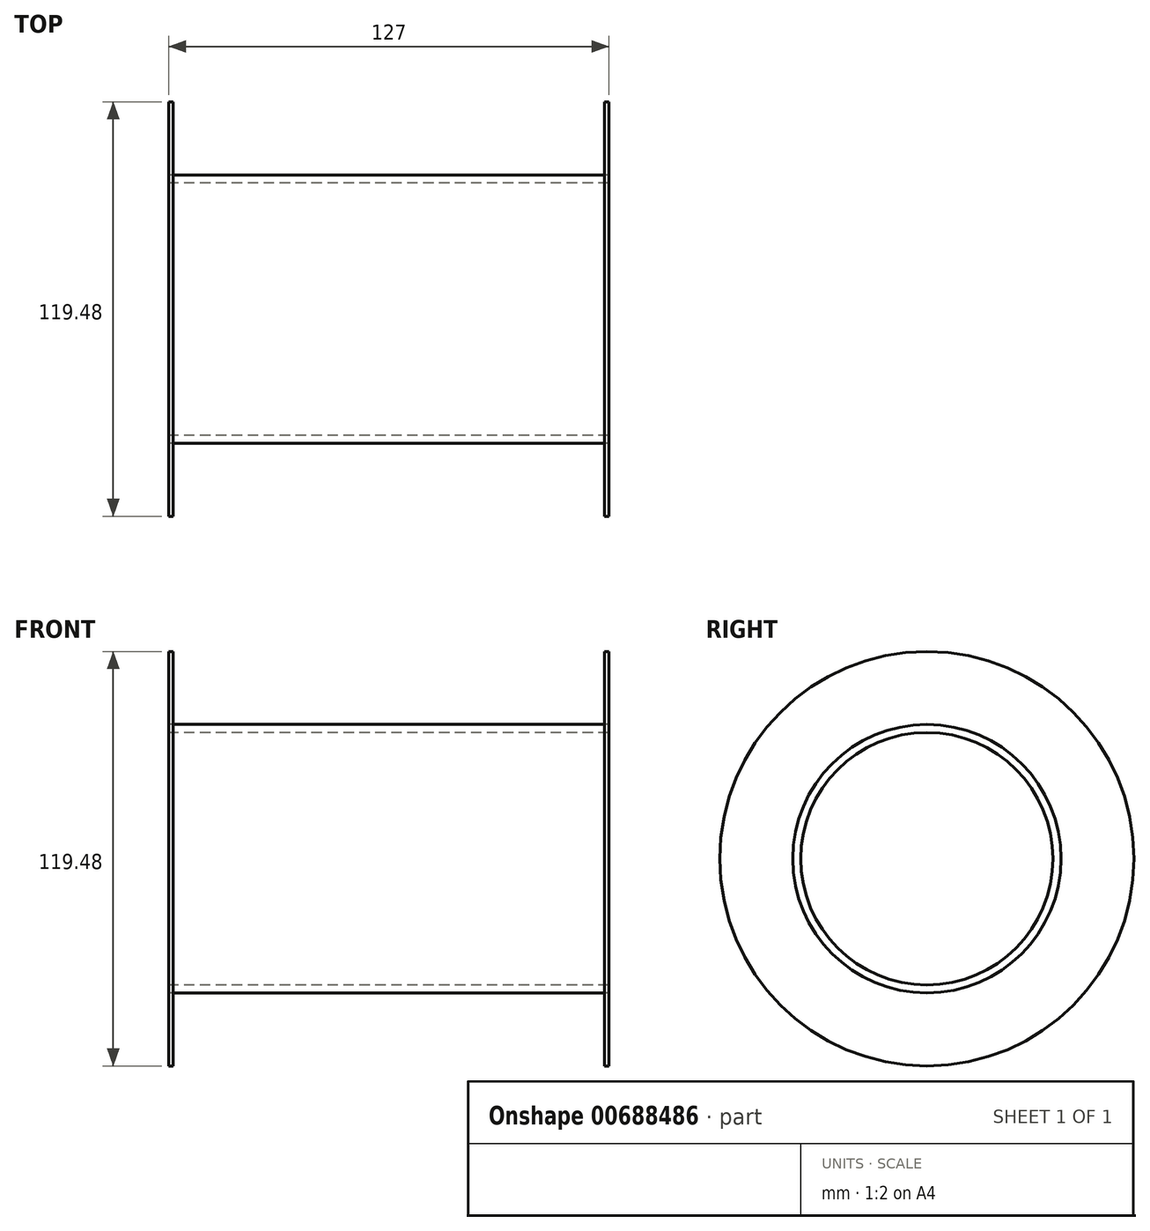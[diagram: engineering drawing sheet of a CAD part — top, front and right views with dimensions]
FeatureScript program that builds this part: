
annotation { "Feature Type Name" : "Feature", "Feature Type Description" : "" }
export const myFeature = defineFeature(function(context is Context, id is Id, definition is map)
    precondition{}
    {
        {
            var Q0;
            Q0=qCreatedBy(makeId("Right.planeOp"),FACE);
            var sketch = newSketch(context, id + "F0", { "sketchPlane" : qUnion([Q0])});
            skCircle(sketch, "E0", {"center": v(0, 0) * mm, "radius": 38.7 * mm});
            skCircle(sketch, "E1", {"center": v(0, 0) * mm, "radius": 36.39 * mm});
            skSolve(sketch);
        }
        {
            var Q0;
            Q0 = qSketchRegion(id + "F0", true);
            extrude(context, id + "F1", {"entities" : qUnion([Q0]), "endBound" : BoundingType.SYMMETRIC, "depth" : 127 * mm, "offsetDistance" : 25.4 * mm});
        }
        {
            var Q0;
            Q0=qCreatedBy(makeId("Front.planeOp"),FACE);
            var sketch = newSketch(context, id + "F2", { "sketchPlane" : qUnion([Q0])});
            skLineSegment(sketch, "E2", {"start": v(-74.68, 0) * mm, "end": v(76.9, 0) * mm, "construction": true});
            skLineSegment(sketch, "E3", {"start": v(0, 0) * mm, "end": v(0, 75.57) * mm, "construction": true});
            skSolve(sketch);
        }
        {
            var Q0;
            Q0=qCreatedBy(makeId("Front.planeOp"),FACE);
            var sketch = newSketch(context, id + "F3", { "sketchPlane" : qUnion([Q0])});
            skLineSegment(sketch, "E4", {"start": v(-73.65, 38.7) * mm, "end": v(68, 38.7) * mm, "construction": true});
            skLineSegment(sketch, "E5.bottom", {"start": v(63.46, 38.7) * mm, "end": v(62.18, 38.7) * mm});
            skLineSegment(sketch, "E5.top", {"start": v(63.46, 59.74) * mm, "end": v(62.18, 59.74) * mm});
            skLineSegment(sketch, "E5.left", {"start": v(63.46, 38.7) * mm, "end": v(63.46, 59.74) * mm});
            skLineSegment(sketch, "E5.right", {"start": v(62.18, 38.7) * mm, "end": v(62.18, 59.74) * mm});
            skLineSegment(sketch, "E6.MirrorCS", {"start": v(-63.46, 59.74) * mm, "end": v(-62.18, 59.74) * mm});
            skLineSegment(sketch, "E7.MirrorCS", {"start": v(-63.46, 38.7) * mm, "end": v(-62.18, 38.7) * mm});
            skLineSegment(sketch, "E8.MirrorCS", {"start": v(-62.18, 38.7) * mm, "end": v(-62.18, 59.74) * mm});
            skLineSegment(sketch, "E9.MirrorCS", {"start": v(-63.46, 38.7) * mm, "end": v(-63.46, 59.74) * mm});
            skSolve(sketch);
        }
        {
            var Q0;
            Q0 = qSketchRegion(id + "F3", true);
            var Q1;
            Q1=sQuery(id+"F2.wireOp",EDGE,"E2");
            revolve(context, id + "F4", {"entities" : qUnion([Q0]), "axis" : qUnion([Q1]), "revolveType" : RevolveType.FULL});
        }
    });
